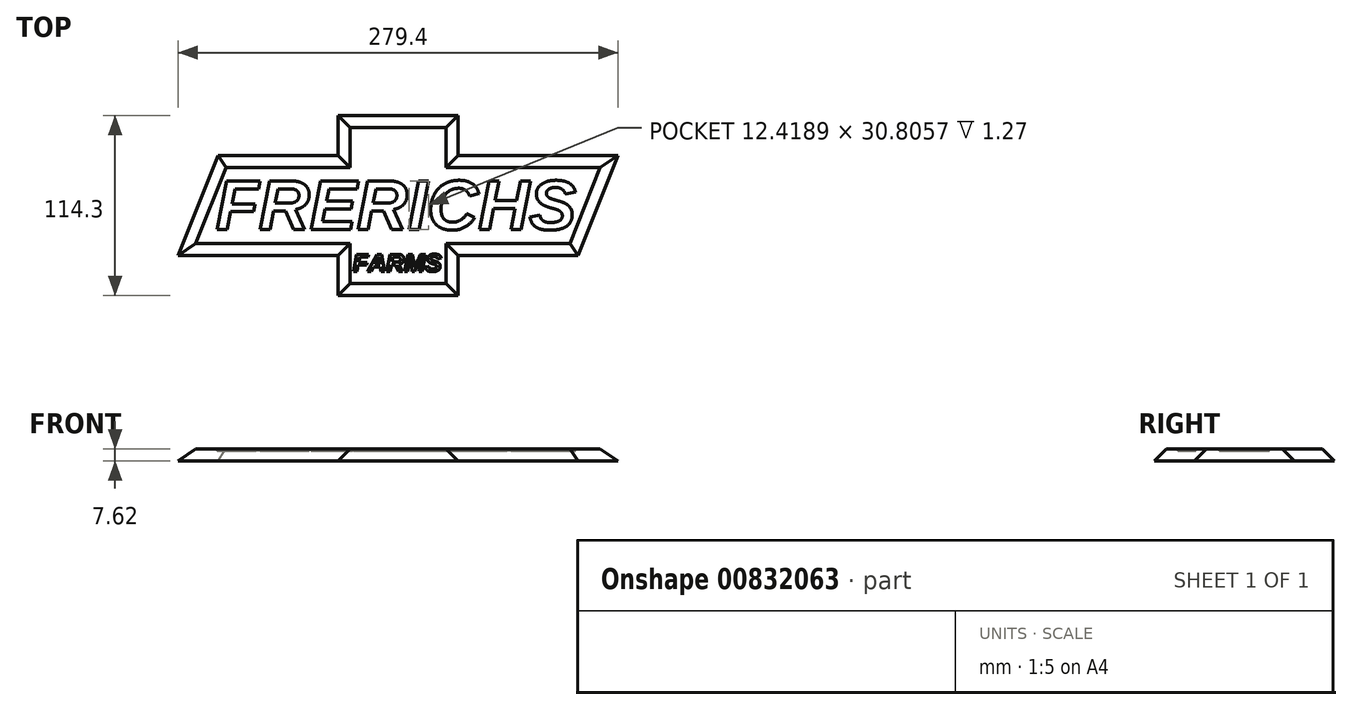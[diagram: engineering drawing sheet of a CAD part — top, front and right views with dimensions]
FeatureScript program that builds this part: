
annotation { "Feature Type Name" : "Feature", "Feature Type Description" : "" }
export const myFeature = defineFeature(function(context is Context, id is Id, definition is map)
    precondition{}
    {
        {
            var Q0;
            Q0=qCreatedBy(makeId("Top.planeOp"),FACE);
            var sketch = newSketch(context, id + "F0", { "sketchPlane" : qUnion([Q0])});
            skLineSegment(sketch, "E0", {"start": v(-139.7, -31.75) * mm, "end": v(-114.3, 31.75) * mm});
            skLineSegment(sketch, "E1", {"start": v(-114.3, 31.75) * mm, "end": v(-38.1, 31.75) * mm});
            skLineSegment(sketch, "E2", {"start": v(-38.1, 31.75) * mm, "end": v(-38.1, 57.15) * mm});
            skLineSegment(sketch, "E3", {"start": v(-38.1, 57.15) * mm, "end": v(38.1, 57.15) * mm});
            skLineSegment(sketch, "E4", {"start": v(38.1, 57.15) * mm, "end": v(38.1, 31.75) * mm});
            skLineSegment(sketch, "E5", {"start": v(38.1, 31.75) * mm, "end": v(139.7, 31.75) * mm});
            skLineSegment(sketch, "E6", {"start": v(139.7, 31.75) * mm, "end": v(114.3, -31.75) * mm});
            skLineSegment(sketch, "E7", {"start": v(114.3, -31.75) * mm, "end": v(38.1, -31.75) * mm});
            skLineSegment(sketch, "E8", {"start": v(38.1, -31.75) * mm, "end": v(38.1, -57.15) * mm});
            skLineSegment(sketch, "E9", {"start": v(38.1, -57.15) * mm, "end": v(-38.1, -57.15) * mm});
            skLineSegment(sketch, "E10", {"start": v(-38.1, -57.15) * mm, "end": v(-38.1, -31.75) * mm});
            skLineSegment(sketch, "E11", {"start": v(-38.1, -31.75) * mm, "end": v(-139.7, -31.75) * mm});
            skSolve(sketch);
        }
        {
            var Q0;
            Q0 = qSketchRegion(id + "F0", true);
            extrude(context, id + "F1", {"entities" : qUnion([Q0]), "depth" : 7.62 * mm, "offsetDistance" : 25.4 * mm});
        }
        {
            var Q0;
            Q0=makeQuery(id+"F1.opExtrude","CAP_FACE",FACE,{"disambiguationData":[OSD([sQuery(id+"F0.wireOp",EDGE,"E0"),sQuery(id+"F0.wireOp",EDGE,"E1"),sQuery(id+"F0.wireOp",EDGE,"E2"),sQuery(id+"F0.wireOp",EDGE,"E3"),sQuery(id+"F0.wireOp",EDGE,"E4"),sQuery(id+"F0.wireOp",EDGE,"E5"),sQuery(id+"F0.wireOp",EDGE,"E6"),sQuery(id+"F0.wireOp",EDGE,"E7"),sQuery(id+"F0.wireOp",EDGE,"E8"),sQuery(id+"F0.wireOp",EDGE,"E9"),sQuery(id+"F0.wireOp",EDGE,"E10"),sQuery(id+"F0.wireOp",EDGE,"E11")])],"isStart":false});
            chamfer(context, id + "F2", {"entities" : qUnion([Q0]), "width" : 7.62 * mm, "tangentPropagation" : true});
        }
        {
            var Q0;
            Q0=makeQuery(id+"F1.opExtrude","CAP_FACE",FACE,{"disambiguationData":[OSD([sQuery(id+"F0.wireOp",EDGE,"E0"),sQuery(id+"F0.wireOp",EDGE,"E1"),sQuery(id+"F0.wireOp",EDGE,"E2"),sQuery(id+"F0.wireOp",EDGE,"E3"),sQuery(id+"F0.wireOp",EDGE,"E4"),sQuery(id+"F0.wireOp",EDGE,"E5"),sQuery(id+"F0.wireOp",EDGE,"E6"),sQuery(id+"F0.wireOp",EDGE,"E7"),sQuery(id+"F0.wireOp",EDGE,"E8"),sQuery(id+"F0.wireOp",EDGE,"E9"),sQuery(id+"F0.wireOp",EDGE,"E10"),sQuery(id+"F0.wireOp",EDGE,"E11")])],"isStart":false});
            var sketch = newSketch(context, id + "F3", { "sketchPlane" : qUnion([Q0])});
            skText(sketch, "E12", { "text": "FRERICHS", "fontName": "Arimo-BoldItalic.ttf"});
            skText(sketch, "E13", { "text": "FARMS", "fontName": "Arimo-BoldItalic.ttf"});
            const initialGuessF3  = {"E12": [-0.11575, -0.01524, 1, 0, 0.03224], "E13": [-0.02857, -0.04187, 1, 0, 0.01139]};
            skSetInitialGuess(sketch, initialGuessF3);
            skSolve(sketch);
        }
        {
            var Q0;
            Q0 = qSketchRegion(id + "F3", true);
            extrude(context, id + "F4", {"entities" : qUnion([Q0]), "operationType" : NewBodyOperationType.REMOVE, "oppositeDirection" : true, "depth" : 1.27 * mm, "offsetDistance" : 25.4 * mm});
        }
    });
